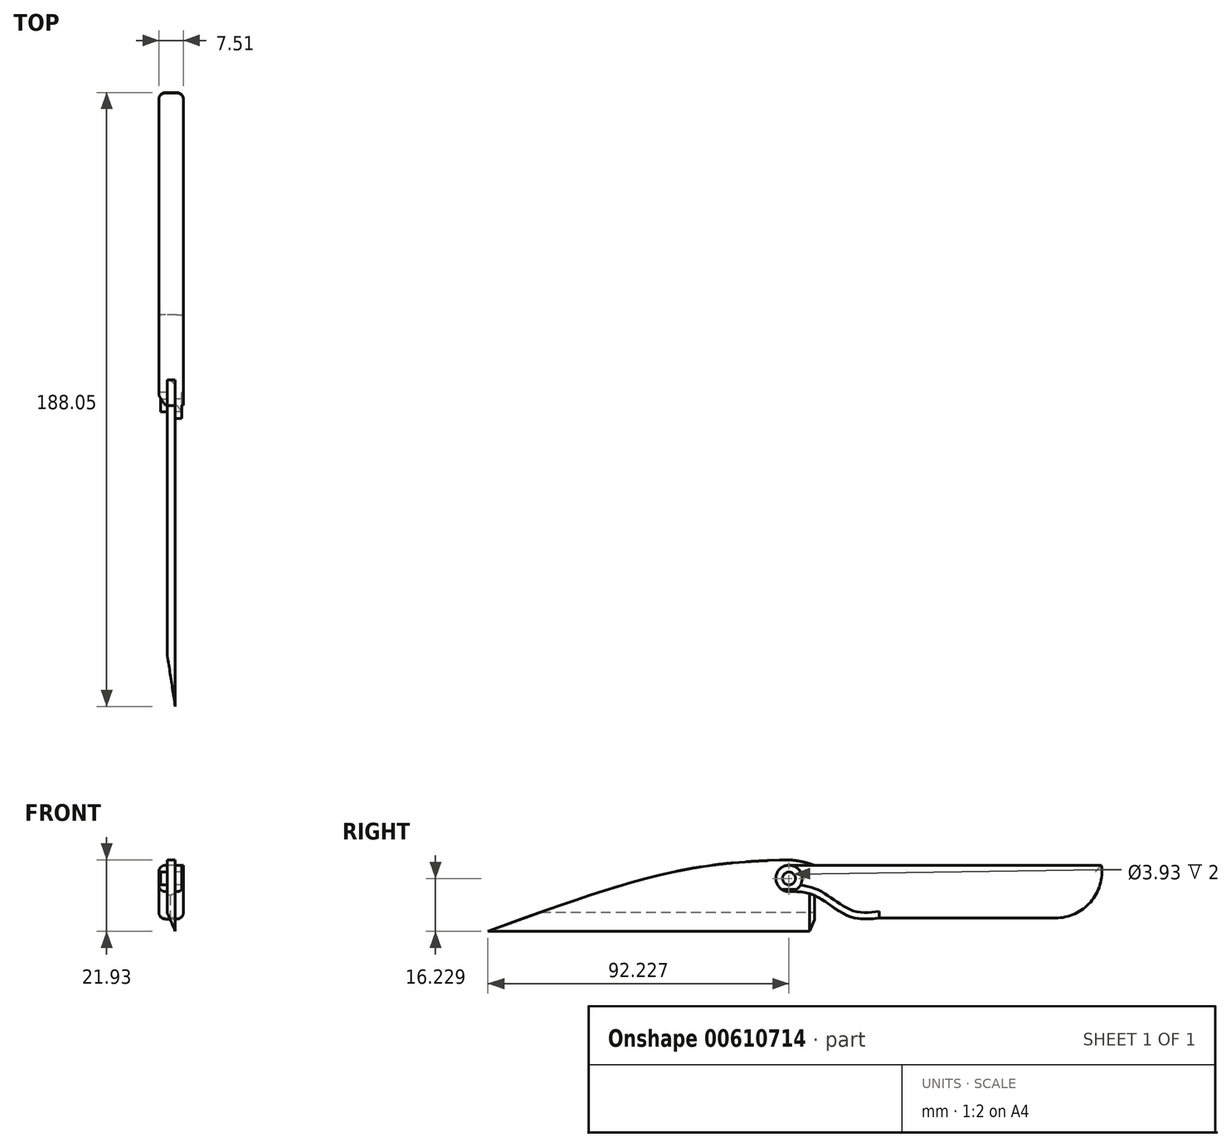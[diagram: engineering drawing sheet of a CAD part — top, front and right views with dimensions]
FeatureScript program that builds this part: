
annotation { "Feature Type Name" : "Feature", "Feature Type Description" : "" }
export const myFeature = defineFeature(function(context is Context, id is Id, definition is map)
    precondition{}
    {
        {
            var Q0;
            Q0=qCreatedBy(makeId("Front.planeOp"),FACE);
            var sketch = newSketch(context, id + "F0", { "sketchPlane" : qUnion([Q0])});
            skLineSegment(sketch, "E0.top", {"start": v(1.25, 25) * mm, "end": v(-1.25, 25) * mm});
            skLineSegment(sketch, "E0.left", {"start": v(1.25, -25) * mm, "end": v(1.25, 25) * mm});
            skLineSegment(sketch, "E0.right", {"start": v(-1.25, -19.1) * mm, "end": v(-1.25, 25) * mm});
            skPoint(sketch, "E0.middle", {"position": v(0, 0) * mm});
            skLineSegment(sketch, "E1", {"start": v(-1.25, -19.1) * mm, "end": v(1.25, -25) * mm});
            skPoint(sketch, "E0.bottom.end.orphan", {"position": v(-1.25, -25) * mm});
            skSolve(sketch);
        }
        {
            var Q0;
            Q0=makeQuery(id+"F0.imprint","IMPRINT",FACE,{"disambiguationData":[TD([[makeQuery(id+"F0.imprint","IMPRINT",EDGE,{"derivedFrom":sQuery(id+"F0.wireOp",EDGE,"E0.top")}),1.0]])]});
            extrude(context, id + "F1", {"entities" : qUnion([Q0]), "depth" : 100 * mm, "offsetDistance" : 25.4 * mm});
        }
        {
            var Q0;
            Q0=makeQuery(id+"F1.opExtrude","SWEPT_FACE",FACE,{"disambiguationData":[OSD([sQuery(id+"F0.wireOp",EDGE,"E0.left")])]});
            var sketch = newSketch(context, id + "F2", { "sketchPlane" : qUnion([Q0])});
            skFitSpline(sketch, "E2", {"points": [v(-100, -25) * mm, v(-78.94, 0) * mm, v(0, 25) * mm], "startDerivative": vector(40.32, 69.43) * mm, "endDerivative": vector(151.24, 33.31) * mm});
            skLineSegment(sketch, "E3", {"start": v(-100, 25) * mm, "end": v(-100, -25) * mm});
            skLineSegment(sketch, "E4", {"start": v(-100, 25) * mm, "end": v(0, 25) * mm});
            skSolve(sketch);
        }
        {
            var Q0;
            Q0=makeQuery(id+"F2.imprint","IMPRINT",FACE,{"disambiguationData":[TD([[makeQuery(id+"F2.imprint","IMPRINT",EDGE,{"derivedFrom":sQuery(id+"F2.wireOp",EDGE,"E2")}),1.0]])]});
            extrude(context, id + "F3", {"entities" : qUnion([Q0]), "operationType" : NewBodyOperationType.REMOVE, "oppositeDirection" : true, "depth" : 25.4 * mm, "offsetDistance" : 25.4 * mm});
        }
        {
            var Q0;
            Q0=makeQuery(id+"F1.opExtrude","SWEPT_FACE",FACE,{"disambiguationData":[OSD([sQuery(id+"F0.wireOp",EDGE,"E0.left")])]});
            var sketch = newSketch(context, id + "F4", { "sketchPlane" : qUnion([Q0])});
            skFitSpline(sketch, "E5", {"points": [v(0, 12.6) * mm, v(-38.83, 4.32) * mm, v(-100, -25) * mm], "startDerivative": vector(-85.6, -12.04) * mm, "endDerivative": vector(-113.18, -61) * mm});
            skSolve(sketch);
        }
        {
            var Q0;
            {var subQ0=sQuery(id+"F4.wireOp",EDGE,"E5");Q0=makeQuery(id+"F4.imprint","IMPRINT",FACE,{"disambiguationData":[TD([[makeQuery(id+"F4.imprint","IMPRINT",EDGE,{"derivedFrom":subQ0}),-1.0]])]});}
            extrude(context, id + "F5", {"entities" : qUnion([Q0]), "operationType" : NewBodyOperationType.REMOVE, "oppositeDirection" : true, "depth" : 25.4 * mm, "offsetDistance" : 25.4 * mm});
        }
        {
            var Q0;
            Q0=makeQuery(id+"F1.opExtrude","SWEPT_FACE",FACE,{"disambiguationData":[OSD([sQuery(id+"F0.wireOp",EDGE,"E0.left")])]});
            var sketch = newSketch(context, id + "F6", { "sketchPlane" : qUnion([Q0])});
            skPoint(sketch, "E6.1.internal.snap0", {"position": v(0, -6.2) * mm});
            skFitSpline(sketch, "E6", {"points": [v(0, -2.92) * mm, v(-40.37, -6.2) * mm, v(-100, -25) * mm], "startDerivative": vector(-86.71, -1.43) * mm, "endDerivative": vector(-112.36, -41.3) * mm});
            skSolve(sketch);
        }
        {
            var Q0;
            {var subQ0=sQuery(id+"F6.wireOp",EDGE,"E6");Q0=makeQuery(id+"F6.imprint","IMPRINT",FACE,{"disambiguationData":[TD([[makeQuery(id+"F6.imprint","IMPRINT",EDGE,{"derivedFrom":subQ0}),-1.0]])]});}
            extrude(context, id + "F7", {"entities" : qUnion([Q0]), "operationType" : NewBodyOperationType.REMOVE, "oppositeDirection" : true, "depth" : 25.4 * mm, "offsetDistance" : 25.4 * mm});
        }
        {
            var Q0;
            Q0=makeQuery(id+"F1.opExtrude","SWEPT_FACE",FACE,{"disambiguationData":[OSD([sQuery(id+"F0.wireOp",EDGE,"E0.left")])]});
            var sketch = newSketch(context, id + "F8", { "sketchPlane" : qUnion([Q0])});
            skCircle(sketch, "E7", {"center": v(-7.77, -8.77) * mm, "radius": 4.04 * mm});
            skCircle(sketch, "E8", {"center": v(-7.77, -8.77) * mm, "radius": 1.96 * mm});
            skSolve(sketch);
        }
        {
            var Q0;
            Q0=makeQuery(id+"F1.opExtrude","SWEPT_FACE",FACE,{"disambiguationData":[OSD([sQuery(id+"F0.wireOp",EDGE,"E0.right")])]});
            var sketch = newSketch(context, id + "F9", { "sketchPlane" : qUnion([Q0])});
            skPoint(sketch, "E9.0", {"position": v(7.77, -8.77) * mm});
            skCircle(sketch, "E10.0", {"center": v(7.77, -8.77) * mm, "radius": 1.96 * mm});
            skCircle(sketch, "E11.0", {"center": v(7.77, -8.77) * mm, "radius": 4.04 * mm});
            skSolve(sketch);
        }
        {
            var Q0;
            Q0=makeQuery(id+"F8.imprint","IMPRINT",FACE,{"disambiguationData":[TD([[makeQuery(id+"F8.imprint","IMPRINT",EDGE,{"derivedFrom":sQuery(id+"F8.wireOp",EDGE,"E7")}),1.0]])]});
            extrude(context, id + "F10", {"entities" : qUnion([Q0]), "operationType" : NewBodyOperationType.ADD, "depth" : 2 * mm, "offsetDistance" : 25.4 * mm});
        }
        {
            var Q0;
            Q0=makeQuery(id+"F9.imprint","IMPRINT",FACE,{"disambiguationData":[TD([[makeQuery(id+"F9.imprint","IMPRINT",EDGE,{"derivedFrom":sQuery(id+"F9.wireOp",EDGE,"E10.0")}),1.0]])]});
            extrude(context, id + "F11", {"entities" : qUnion([Q0]), "operationType" : NewBodyOperationType.ADD, "depth" : 2 * mm, "offsetDistance" : 25.4 * mm});
        }
        {
            var Q0;
            {var subQ0=sQuery(id+"F0.wireOp",EDGE,"E1");var subQ1=sQuery(id+"F0.wireOp",EDGE,"E0.left");Q0=makeQuery(id+"F10.boolean.opBoolean","SPLIT",FACE,{"disambiguationData":[TD([makeQuery(id+"F1.opExtrude","SWEPT_FACE",FACE,{"disambiguationData":[OSD([subQ0])]})])],"derivedFrom":makeQuery(id+"F1.opExtrude","SWEPT_FACE",FACE,{"disambiguationData":[OSD([subQ1])]})});}
            var sketch = newSketch(context, id + "F12", { "sketchPlane" : qUnion([Q0])});
            skFitSpline(sketch, "E12", {"points": [v(-7.74, -12.81) * mm, v(0, -13.96) * mm, v(10.6, -20.34) * mm, v(19.94, -20.9) * mm], "startDerivative": vector(25.41, 0.29) * mm, "endDerivative": vector(28.57, 3.09) * mm});
            skLineSegment(sketch, "E13", {"start": v(-7.77, -4.73) * mm, "end": v(87.91, -4.73) * mm});
            skLineSegment(sketch, "E14", {"start": v(19.94, -20.9) * mm, "end": v(73.87, -20.9) * mm});
            skArc(sketch, "E15", {"start": v(73.87, -20.9) * mm, "mid": v(84.58, -16.01) * mm, "end": v(87.91, -4.73) * mm});
            skArc(sketch, "E16", {"start": v(-7.77, -4.73) * mm, "mid": v(-11.8, -8.78) * mm, "end": v(-7.74, -12.81) * mm});
            skSolve(sketch);
        }
        {
            var Q0;
            {var subQ0=sQuery(id+"F12.wireOp",EDGE,"E14");Q0=makeQuery(id+"F12.imprint","IMPRINT",FACE,{"disambiguationData":[TD([[makeQuery(id+"F12.imprint","IMPRINT",EDGE,{"derivedFrom":subQ0}),1.0]])]});}
            var Q1;
            {var subQ0=sQuery(id+"F12.wireOp",EDGE,"E12");var subQ1=makeQuery(id+"F10.opExtrude","CAP_EDGE",EDGE,{"disambiguationData":[OSD([sQuery(id+"F8.wireOp",EDGE,"E7")])],"isStart":true});var subQ2=makeQuery(id+"F12.imprint","INTERSECT",VERTEX,{"derivedFrom":[subQ1,subQ0]});Q1=makeQuery(id+"F12.imprint","IMPRINT",FACE,{"disambiguationData":[TD([[makeQuery(id+"F12.imprint","IMPRINT",EDGE,{"disambiguationData":[TD([[subQ2,-1.0]])],"derivedFrom":subQ0}),1.0]])]});}
            extrude(context, id + "F13", {"entities" : qUnion([Q0, Q1]), "operationType" : NewBodyOperationType.ADD, "endBound" : BoundingType.SYMMETRIC, "depth" : 10 * mm, "offsetDistance" : 25.4 * mm});
        }
        {
            var Q0;
            Q0=makeQuery(id+"F13.opExtrude","SWEPT_FACE",FACE,{"disambiguationData":[OSD([sQuery(id+"F12.wireOp",EDGE,"E13")])]});
            var sketch = newSketch(context, id + "F14", { "sketchPlane" : qUnion([Q0])});
            skLineSegment(sketch, "E17", {"start": v(3.76, -7.77) * mm, "end": v(3.76, 89.38) * mm});
            skLineSegment(sketch, "E18", {"start": v(3.76, 89.38) * mm, "end": v(12, 89.38) * mm});
            skLineSegment(sketch, "E19", {"start": v(12, 89.38) * mm, "end": v(12, -7.73) * mm});
            skLineSegment(sketch, "E20", {"start": v(12, -7.73) * mm, "end": v(12, -10.8) * mm});
            skLineSegment(sketch, "E21", {"start": v(12, -10.8) * mm, "end": v(3.76, -7.77) * mm});
            skSolve(sketch);
        }
        {
            var Q0;
            {var subQ6=sQuery(id+"F14.wireOp",EDGE,"E18");Q0=makeQuery(id+"F14.imprint","IMPRINT",FACE,{"disambiguationData":[TD([[makeQuery(id+"F14.imprint","IMPRINT",EDGE,{"derivedFrom":subQ6}),-1.0]])]});}
            var Q1;
            {var subQ1=sQuery(id+"F12.wireOp",EDGE,"E13");var subQ10=makeQuery(id+"F13.opExtrude","CAP_EDGE",EDGE,{"disambiguationData":[OSD([subQ1])],"isStart":false});Q1=makeQuery(id+"F14.imprint","IMPRINT",FACE,{"disambiguationData":[TD([[makeQuery(id+"F14.imprint","IMPRINT",EDGE,{"derivedFrom":subQ10}),1.0]])]});}
            extrude(context, id + "F15", {"entities" : qUnion([Q0, Q1]), "operationType" : NewBodyOperationType.REMOVE, "oppositeDirection" : true, "depth" : 25.4 * mm, "offsetDistance" : 25.4 * mm});
        }
        {
            var Q0;
            Q0=makeQuery(id+"F15.boolean.opBoolean","INTERSECT",EDGE,{"derivedFrom":[makeQuery(id+"F13.opExtrude","SWEPT_FACE",FACE,{"disambiguationData":[OSD([sQuery(id+"F12.wireOp",EDGE,"E14")])]}),makeQuery(id+"F15.opExtrude","SWEPT_FACE",FACE,{"disambiguationData":[OSD([sQuery(id+"F14.wireOp",EDGE,"E17")])]})]});
            var Q1;
            Q1=makeQuery(id+"F15.boolean.opBoolean","INTERSECT",EDGE,{"derivedFrom":[makeQuery(id+"F13.opExtrude","SWEPT_FACE",FACE,{"disambiguationData":[OSD([sQuery(id+"F12.wireOp",EDGE,"E12")])]}),makeQuery(id+"F15.opExtrude","SWEPT_FACE",FACE,{"disambiguationData":[OSD([sQuery(id+"F14.wireOp",EDGE,"E17")])]})]});
            var Q2;
            Q2=makeQuery(id+"F13.opExtrude","CAP_EDGE",EDGE,{"disambiguationData":[OSD([sQuery(id+"F12.wireOp",EDGE,"E12")])],"isStart":true});
            var Q3;
            Q3=makeQuery(id+"F13.opExtrude","CAP_EDGE",EDGE,{"disambiguationData":[OSD([sQuery(id+"F12.wireOp",EDGE,"E14")])],"isStart":true});
            var Q4;
            Q4=makeQuery(id+"F13.opExtrude","CAP_EDGE",EDGE,{"disambiguationData":[OSD([sQuery(id+"F12.wireOp",EDGE,"E13")])],"isStart":true});
            var Q5;
            Q5=makeQuery(id+"F15.boolean.opBoolean","COPY",EDGE,{"derivedFrom":makeQuery(id+"F15.opExtrude","CAP_EDGE",EDGE,{"disambiguationData":[OSD([sQuery(id+"F14.wireOp",EDGE,"E17")])],"isStart":true})});
            fillet(context, id + "F16", {"entities" : qUnion([Q0, Q1, Q2, Q3, Q4, Q5]), "radius" : 2 * mm, "tangentPropagation" : true, "allowEdgeOverflow" : false});
        }
        {
            var Q0;
            {var subQ0=sQuery(id+"F0.wireOp",EDGE,"E1");var subQ1=sQuery(id+"F0.wireOp",EDGE,"E0.right");Q0=makeQuery(id+"F11.boolean.opBoolean","SPLIT",FACE,{"disambiguationData":[TD([makeQuery(id+"F1.opExtrude","SWEPT_FACE",FACE,{"disambiguationData":[OSD([subQ0])]})])],"derivedFrom":makeQuery(id+"F1.opExtrude","SWEPT_FACE",FACE,{"disambiguationData":[OSD([subQ1])]})});}
            var sketch = newSketch(context, id + "F17", { "sketchPlane" : qUnion([Q0])});
            skFitSpline(sketch, "E22", {"points": [v(7.86, -3.07) * mm, v(3.8, -3.62) * mm, v(0, -4.73) * mm], "startDerivative": vector(-8.15, -0.63) * mm, "endDerivative": vector(-7.58, -2.55) * mm});
            skLineSegment(sketch, "E23", {"start": v(0, -4.73) * mm, "end": v(0, -2.92) * mm});
            skLineSegment(sketch, "E24", {"start": v(0, -2.92) * mm, "end": v(7.86, -3.07) * mm});
            skSolve(sketch);
        }
        {
            var Q0;
            Q0=makeQuery(id+"F17.imprint","IMPRINT",FACE,{"disambiguationData":[TD([[makeQuery(id+"F17.imprint","IMPRINT",EDGE,{"derivedFrom":sQuery(id+"F17.wireOp",EDGE,"E22")}),-1.0]])]});
            extrude(context, id + "F18", {"entities" : qUnion([Q0]), "operationType" : NewBodyOperationType.REMOVE, "oppositeDirection" : true, "depth" : 25.4 * mm, "offsetDistance" : 25.4 * mm});
        }
        {
            var Q0;
            {var subQ0=sQuery(id+"F0.wireOp",EDGE,"E1");var subQ1=sQuery(id+"F0.wireOp",EDGE,"E0.left");Q0=makeQuery(id+"F13.boolean.opBoolean","SPLIT",EDGE,{"disambiguationData":[TD([makeQuery(id+"F1.opExtrude","SWEPT_FACE",FACE,{"disambiguationData":[OSD([subQ0])]})])],"derivedFrom":makeQuery(id+"F1.opExtrude","CAP_EDGE",EDGE,{"disambiguationData":[OSD([subQ1])],"isStart":true})});}
            chamfer(context, id + "F19", {"entities" : qUnion([Q0]), "width" : 1.5 * mm, "tangentPropagation" : true});
        }
    });
